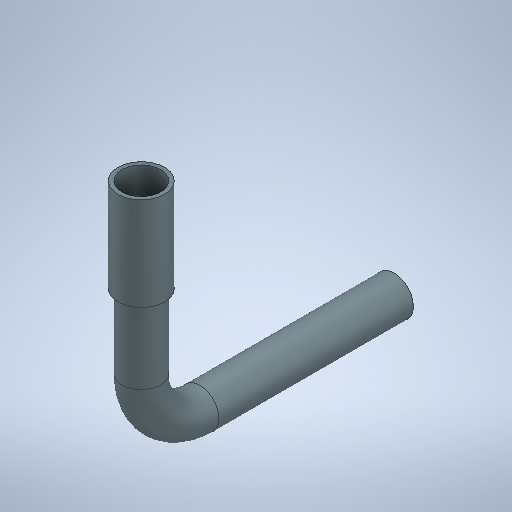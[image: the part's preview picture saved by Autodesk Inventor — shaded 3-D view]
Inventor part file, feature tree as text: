
AUTODESK INVENTOR PART (.ipt)
format: ipt  version: 2025.1 (Build 291241000, 241)  size: 300,032 bytes
history: native  units: mm
features: sketch x3, sweep x1, extrude x1, shell x1
ambient origin geometry x8: Origin, YZ Plane, XZ Plane, XY Plane, X Axis, Y Axis, Z Axis, Center Point
bodies: Solid1 (feature_tree)
feature tree (6):
  sweep  "Sweep1"
  extrude  "Extrusion1"  Depth=7.5mm
  shell  "Shell1"  Thickness=0.0mm
  sketch  "Sketch1"  dims[d0=5.0mm d1=23.0mm]
  sketch  "Sketch2"  dims[d2=7.5mm d3=25.0mm d4=0.0mm d5=0.0mm]
  sketch  "Sketch3"  dims[d6=6.0mm d7=12.0mm d8=0.0mm d9=0.5mm]
